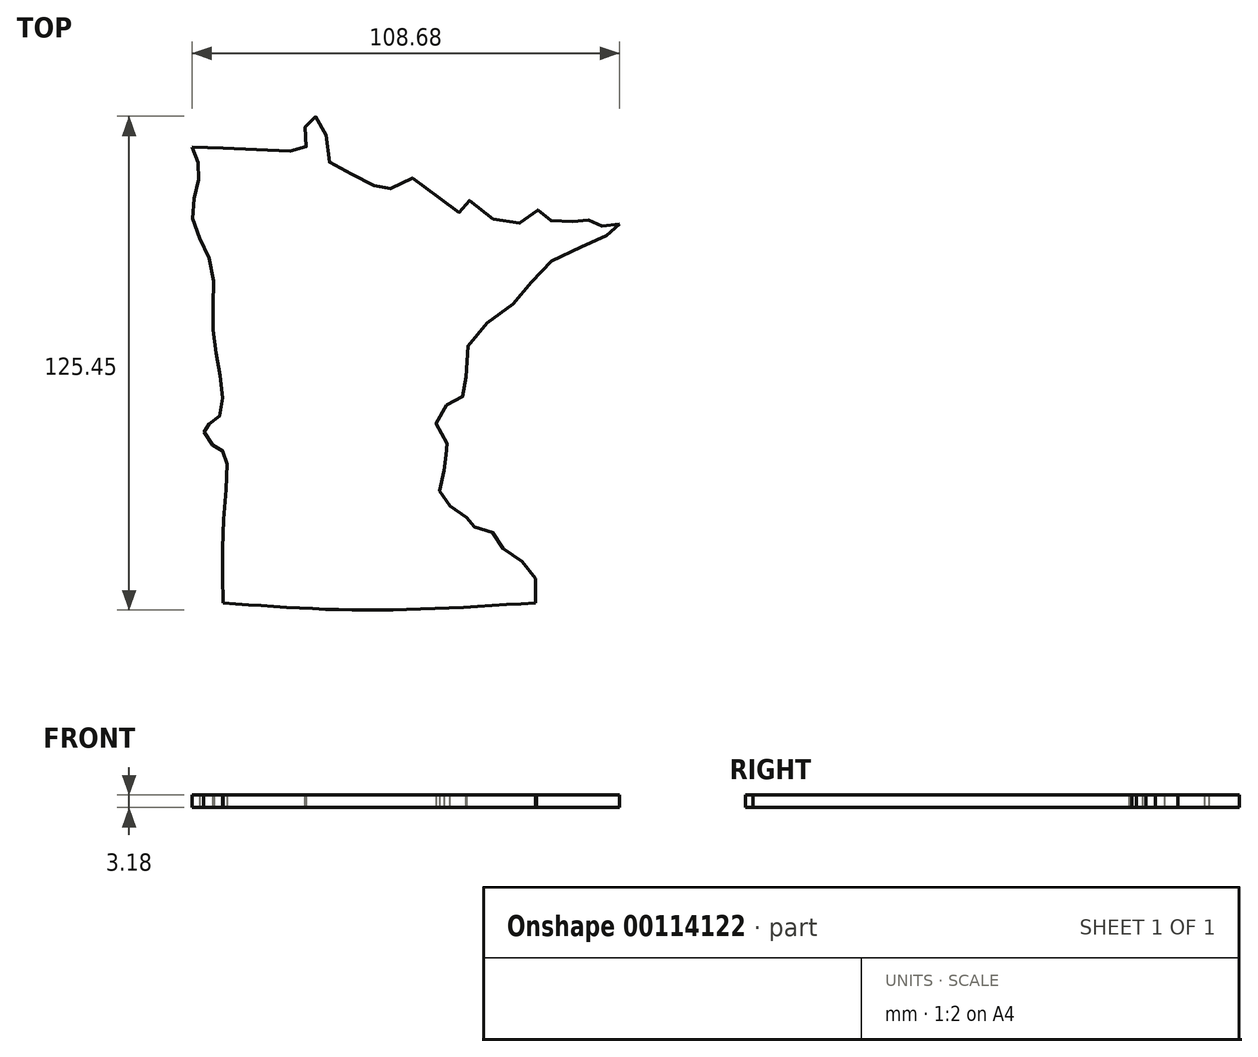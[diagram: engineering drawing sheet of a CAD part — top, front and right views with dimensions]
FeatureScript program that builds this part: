
annotation { "Feature Type Name" : "Feature", "Feature Type Description" : "" }
export const myFeature = defineFeature(function(context is Context, id is Id, definition is map)
    precondition{}
    {
        {
            var Q0;
            Q0=qCreatedBy(makeId("Top.planeOp"),FACE);
            var sketch = newSketch(context, id + "F0", { "sketchPlane" : qUnion([Q0])});
            skFitSpline(sketch, "E0", {"points": [v(-41.11, 55.64) * mm, v(-25.8, 55.03) * mm, v(-12.9, 55.03) * mm, v(-12.09, 56.65) * mm, v(-11.89, 62.9) * mm, v(-7.86, 62.09) * mm, v(-6.24, 51.8) * mm, v(2.83, 47.58) * mm, v(8.07, 44.55) * mm, v(15.32, 47.78) * mm, v(26.4, 38.91) * mm, v(28.82, 42.14) * mm, v(39.3, 35.48) * mm, v(46.56, 39.72) * mm, v(49.79, 37.1) * mm, v(56.44, 36.9) * mm, v(59.86, 37.1) * mm, v(62.89, 35.69) * mm, v(67.52, 36.09) * mm], "startDerivative": vector(176.9, -5.25) * mm, "endDerivative": vector(109.1, 24.93) * mm});
            skFitSpline(sketch, "E1", {"points": [v(-41.11, 55.64) * mm, v(-39.3, 48.38) * mm, v(-41.11, 37.9) * mm, v(-36.27, 26.01) * mm, v(-35.87, 9.89) * mm, v(-33.65, -4.62) * mm, v(-34.86, -13.7) * mm, v(-38.09, -15.7) * mm, v(-35.47, -20.34) * mm, v(-32.85, -22.16) * mm, v(-33.05, -38.89) * mm, v(-33.24, -60.14) * mm], "startDerivative": vector(38.85, -88.35) * mm, "endDerivative": vector(3.77, -155.03) * mm});
            skFitSpline(sketch, "E2", {"points": [v(-33.24, -60.14) * mm, v(2.82, -61.96) * mm, v(46.17, -60.14) * mm], "startDerivative": vector(73.84, -5.57) * mm, "endDerivative": vector(84.82, 5.4) * mm});
            skFitSpline(sketch, "E3", {"points": [v(46.17, -60.14) * mm, v(45.08, -51.5) * mm, v(37.97, -46.51) * mm, v(34.68, -41.8) * mm, v(29.52, -40.47) * mm, v(28.28, -37.8) * mm, v(22.05, -33.7) * mm, v(22.73, -27.55) * mm, v(23.17, -22.99) * mm, v(24.28, -21.08) * mm, v(20.9, -14.95) * mm, v(24.76, -9) * mm, v(28.24, -6.94) * mm, v(29.09, 5.6) * mm, v(40.64, 15.93) * mm, v(49.4, 26.15) * mm, v(63.4, 32.74) * mm, v(67.52, 36.09) * mm], "startDerivative": vector(12.48, 139.41) * mm, "endDerivative": vector(56.13, 62.14) * mm});
            skSolve(sketch);
        }
        {
            var Q0;
            Q0 = qSketchRegion(id + "F0", true);
            extrude(context, id + "F1", {"entities" : qUnion([Q0]), "depth" : 3.17 * mm});
        }
    });
